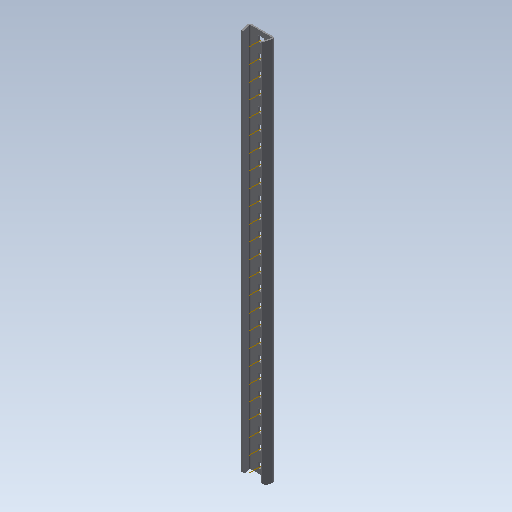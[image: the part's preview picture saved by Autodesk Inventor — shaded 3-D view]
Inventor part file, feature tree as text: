
AUTODESK INVENTOR PART (.ipt)
format: ipt  version: 2020 (Build 240168000, 168)  size: 442,880 bytes
history: native  units: in
note: dims shown in document units (in); Inventor stores cm internally (conversion verified against a paired STEP export)
features: other x28, boolean_combine x1, extrude x1, pattern_linear x1, plane x1, imported_body x1, sketch x1
ambient origin geometry x8: Origin, YZ Plane, XZ Plane, XY Plane, X Axis, Y Axis, Z Axis, Center Point
bodies: Body1 (feature_tree)
feature tree (34):
  boolean_combine  "Combine1"
  other  "Linear Slide"
  other  "Work Axis1"
  extrude  "Extrusion1"  TaperAngle=0.0deg  [1 undecoded]
  pattern_linear  "Rectangular Pattern1"  Spacing1=0.0in  [1 undecoded]
  plane  "Work Plane3"
  imported_body  "Base1"
  other  "Work Point1"
  other  "Work Axis2"
  sketch  "Sketch1"  dims[d0=9.8425in d2=0.5in d4=0.0in d5=0.0in d6=0.0in d9=-12.5in d10=0.0in]
  other  "Work Axis46"
  other  "Work Axis47"
  other  "Work Axis48"
  other  "Work Axis49"
  other  "Work Axis50"
  other  "Work Axis51"
  other  "Work Axis52"
  other  "Work Axis53"
  other  "Work Axis54"
  other  "Work Axis55"
  other  "Work Axis56"
  other  "Work Axis57"
  other  "Work Axis69"
  other  "Work Axis70"
  other  "Work Axis71"
  other  "Work Axis72"
  other  "Work Axis73"
  other  "Work Axis74"
  other  "Work Axis75"
  other  "Work Axis76"
  other  "Work Axis77"
  other  "Work Axis78"
  other  "bottom plane"
  other  "Work Axis90"
note: 2 required parameter values undecoded (feature->parameter linkage not recoverable at this tier; creation-order binding heuristic only, values carry confidence <= 0.55)
